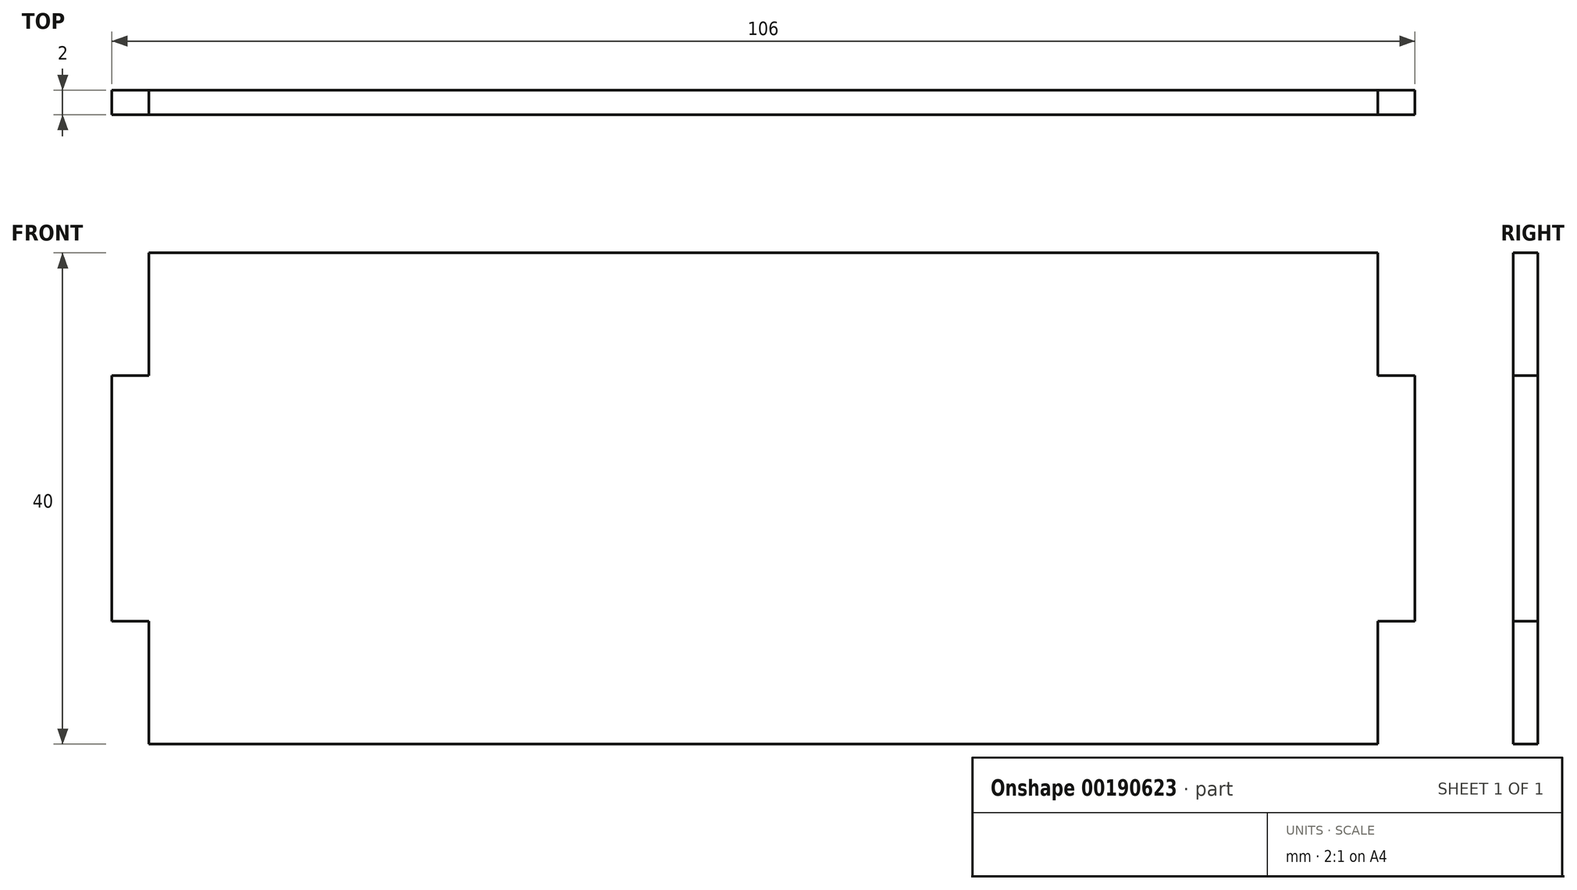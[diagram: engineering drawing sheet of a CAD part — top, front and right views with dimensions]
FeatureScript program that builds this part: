
annotation { "Feature Type Name" : "Feature", "Feature Type Description" : "" }
export const myFeature = defineFeature(function(context is Context, id is Id, definition is map)
    precondition{}
    {
        {
            var Q0;
            Q0=qCreatedBy(makeId("Front.planeOp"),FACE);
            var sketch = newSketch(context, id + "F0", { "sketchPlane" : qUnion([Q0])});
            skSolve(sketch);
        }
        {
            var Q0;
            Q0=qCreatedBy(makeId("Front.planeOp"),FACE);
            var sketch = newSketch(context, id + "F1", { "sketchPlane" : qUnion([Q0])});
            skLineSegment(sketch, "E0.bottom", {"start": v(50, -20) * mm, "end": v(-50, -20) * mm});
            skLineSegment(sketch, "E0.top", {"start": v(50, 20) * mm, "end": v(-50, 20) * mm});
            skLineSegment(sketch, "E0.left", {"start": v(50, -20) * mm, "end": v(50, -10) * mm});
            skPoint(sketch, "E0.middle", {"position": v(0, 0) * mm});
            skLineSegment(sketch, "E1.bottom", {"start": v(50, -10) * mm, "end": v(53, -10) * mm});
            skLineSegment(sketch, "E1.top", {"start": v(50, 10) * mm, "end": v(53, 10) * mm});
            skLineSegment(sketch, "E1.left", {"start": v(50, -10) * mm, "end": v(50, -10) * mm});
            skLineSegment(sketch, "E1.right", {"start": v(53, -10) * mm, "end": v(53, 10) * mm});
            skLineSegment(sketch, "E2", {"start": v(0, 20) * mm, "end": v(0, -20) * mm, "construction": true});
            skLineSegment(sketch, "E3", {"start": v(50, 10) * mm, "end": v(50, 10) * mm});
            skLineSegment(sketch, "E4", {"start": v(50, 10) * mm, "end": v(50, 20) * mm});
            skLineSegment(sketch, "E5.MirrorCS", {"start": v(-50, 10) * mm, "end": v(-53, 10) * mm});
            skLineSegment(sketch, "E6.MirrorCS", {"start": v(-50, -20) * mm, "end": v(-50, -10) * mm});
            skLineSegment(sketch, "E7.MirrorCS", {"start": v(-50, 10) * mm, "end": v(-50, 20) * mm});
            skLineSegment(sketch, "E8.MirrorCS", {"start": v(-50, -10) * mm, "end": v(-53, -10) * mm});
            skLineSegment(sketch, "E9.MirrorCS", {"start": v(-53, -10) * mm, "end": v(-53, 10) * mm});
            skSolve(sketch);
        }
        {
            var Q0;
            Q0=makeQuery(id+"F1.imprint","IMPRINT",FACE,{"disambiguationData":[TD([[makeQuery(id+"F1.imprint","IMPRINT",EDGE,{"derivedFrom":sQuery(id+"F1.wireOp",EDGE,"E0.bottom")}),-1.0]])]});
            var Q1;
            Q1 = qSketchRegion(id + "F0", true);
            extrude(context, id + "F2", {"entities" : qUnion([Q0, Q1]), "depth" : 2 * mm});
        }
    });
